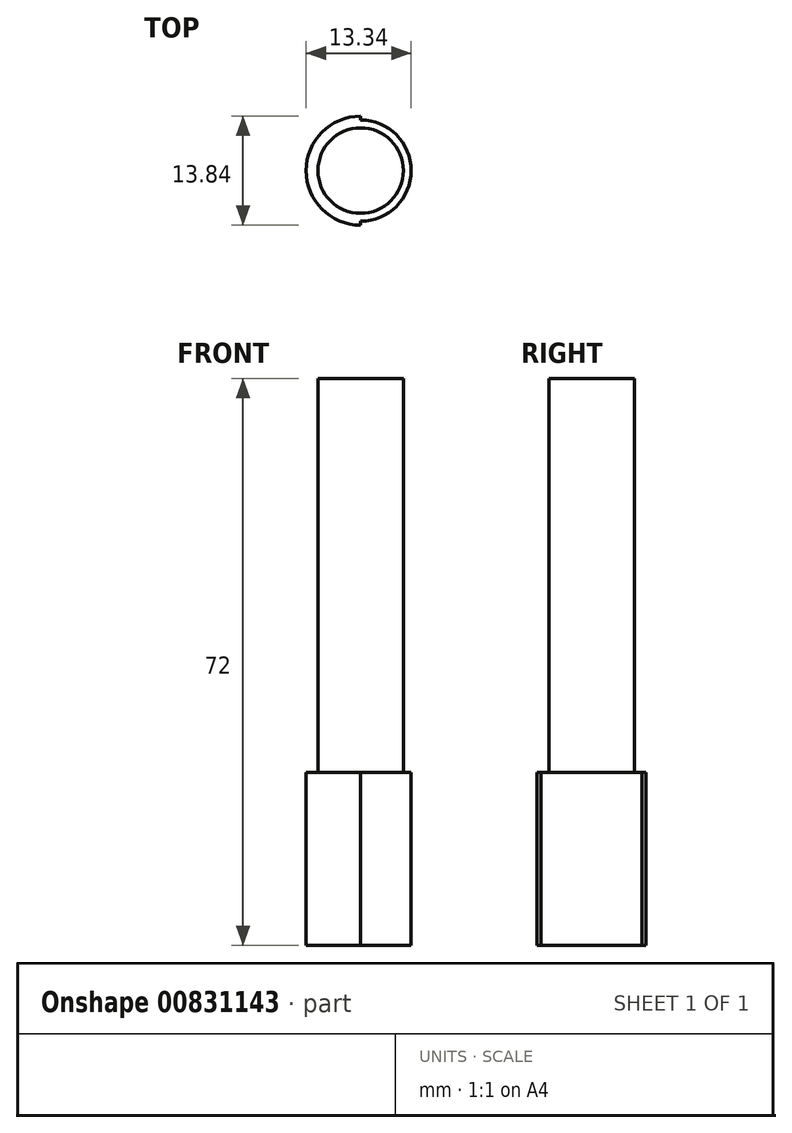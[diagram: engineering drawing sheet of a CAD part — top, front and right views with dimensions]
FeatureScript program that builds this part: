
annotation { "Feature Type Name" : "Feature", "Feature Type Description" : "" }
export const myFeature = defineFeature(function(context is Context, id is Id, definition is map)
    precondition{}
    {
        {
            var Q0;
            Q0=qCreatedBy(makeId("Front.planeOp"),FACE);
            var sketch = newSketch(context, id + "F0", { "sketchPlane" : qUnion([Q0])});
            skLineSegment(sketch, "E0", {"start": v(0, 0) * mm, "end": v(5.42, 0) * mm});
            skLineSegment(sketch, "E1", {"start": v(5.42, 0) * mm, "end": v(5.42, -50) * mm});
            skLineSegment(sketch, "E2", {"start": v(5.42, -50) * mm, "end": v(6.43, -50) * mm});
            skLineSegment(sketch, "E3", {"start": v(6.43, -50) * mm, "end": v(6.43, -72) * mm});
            skLineSegment(sketch, "E4", {"start": v(6.43, -72) * mm, "end": v(0, -72) * mm});
            skLineSegment(sketch, "E5", {"start": v(0, -72) * mm, "end": v(0, 0) * mm});
            skSolve(sketch);
        }
        {
            var Q0;
            Q0=makeQuery(id+"F0.imprint","IMPRINT",FACE,{"disambiguationData":[TD([[makeQuery(id+"F0.imprint","IMPRINT",EDGE,{"derivedFrom":sQuery(id+"F0.wireOp",EDGE,"E0")}),-1.0]])]});
            var Q1;
            Q1=sQuery(id+"F0.wireOp",EDGE,"E5");
            revolve(context, id + "F1", {"surfaceOperationType" : NewSurfaceOperationType.NEW, "entities" : qUnion([Q0]), "axis" : qUnion([Q1]), "revolveType" : RevolveType.SYMMETRIC, "angle" : 180 * degree});
        }
        {
            var Q0;
            Q0=qCreatedBy(makeId("Front.planeOp"),FACE);
            var sketch = newSketch(context, id + "F2", { "sketchPlane" : qUnion([Q0])});
            skLineSegment(sketch, "E6", {"start": v(0, 0) * mm, "end": v(-5.42, 0) * mm});
            skLineSegment(sketch, "E7", {"start": v(-5.42, 0) * mm, "end": v(-5.42, -50) * mm});
            skLineSegment(sketch, "E8", {"start": v(-5.42, -50) * mm, "end": v(-6.92, -50) * mm});
            skLineSegment(sketch, "E9", {"start": v(-6.92, -50) * mm, "end": v(-6.92, -72) * mm});
            skLineSegment(sketch, "E10", {"start": v(-6.92, -72) * mm, "end": v(0, -72) * mm});
            skLineSegment(sketch, "E11", {"start": v(0, -72) * mm, "end": v(0, 0) * mm});
            skSolve(sketch);
        }
        {
            var Q0;
            Q0=makeQuery(id+"F2.imprint","IMPRINT",FACE,{"disambiguationData":[TD([[makeQuery(id+"F2.imprint","IMPRINT",EDGE,{"derivedFrom":sQuery(id+"F2.wireOp",EDGE,"E6")}),1.0]])]});
            var Q1;
            Q1=sQuery(id+"F2.wireOp",EDGE,"E11");
            revolve(context, id + "F3", {"operationType" : NewBodyOperationType.ADD, "surfaceOperationType" : NewSurfaceOperationType.NEW, "entities" : qUnion([Q0]), "axis" : qUnion([Q1]), "revolveType" : RevolveType.SYMMETRIC, "angle" : 180 * degree});
        }
    });
